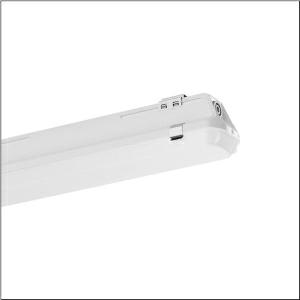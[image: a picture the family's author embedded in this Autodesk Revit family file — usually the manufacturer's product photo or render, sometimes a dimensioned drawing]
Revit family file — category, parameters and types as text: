
# Revit family: monsun_r__21_51fb107p430j005_42d6
name_source: partatom
category: Lighting Fixtures
units: mm (PartAtom-declared; Revit-internal decimal feet)

## family parameters
Cut with Voids When Loaded = No
Host = Face
Light Source = No
Part Type = Normal
Room Calculation Point = No
Round Connector Dimension = Use Diameter
Shared = No

## types (1)
- Monsun® 21 (1 x LED, 3710 lm, 22.2 W, 4000K)
    Apparent Load = 22 VA
    CIE Flux Codes = 47 77 93 94 100
    Color Rendering = 80
    Color Temperature = 4000K
    Default Elevation = 1800 mm
    Description = Monsun® 21, damp-proof luminaire, chain hanger, primary optical cover: enclosure, of PMMA, light emission: direct distribution, primary light characteristic: symmetric, installation type: suspended mounting, surface-mounted, horizontal mounting, vertical mounting, LED, rated luminous flux: 3.710lm, luminous efficacy: 167lm/W, light colour: 840, colour temperature: 4000K, control gear: ECG, with terminal, 3-pole, max. 2.5mm², through-wiring: 5x 2.5mm², mains connection: 220..240V, AC, 50/60Hz, rated input power: 22W, housing, of glass-fibre reinforced polyester, uncoated, bright grey, incl. chain hanger, length: 1.590mm, width: 90mm, height: 88mm, clip for enclosure, of stainless steel (V2A), ceiling mounting element, of stainless steel (V2A), chain hanger, of stainless steel (V2A), protection rating (complete): IP66, insulation class (complete): insulation class I (protective earthing), certification: CE, ENEC, VDE, UKCA, protection symbol: D, impact resistance: IK04, permissible operating ambient temperature: -25..+35°C, standard: EN 50419, EN 60598-2-1, corresponds to IFS (International Featured Standards) requirements for safety and quality in the food industry, for indoor or canopied outdoor use, no direct snow, no direct sun, no direct rain, contact your sales advisor before using the luminaires in applications with unclear chemical exposure, large temperature fluctuations or condensation-forming humidity, LABS conformity tested according to VDMA 24364:2018-05, packaging unit: 1 piece
    Height = 89 mm
    Lamp = 1 x LED
    Lamp Light Flux = 3710 lm
    Lamp Power = 22.2 W
    Lamp count = 1
    Length = 1590 mm
    Luminous efficacy = 167 lm/W
    Manufacturer = Siteco
    ModVariant = No
    Model = 51FB107P430J005
    Mounting Place = Ceiling
    Mounting Type = Surface mounted
    Number of Poles = 1
    OnlyDefault = Yes
    Power Factor = 1
    Product Name = Monsun® 21
    Product group = damp-proof luminaire
    ProductGroupID = 300
    Protection Class = Protection class I
    Protection Degree = IP 66
    RLX_Detail_Level = 1
    RLX_Emergency_Light_Flux = 0 lm
    RLX_Emergency_Type = 0
    RLX_Emergency_Type_DB = No
    RlxData = <blob elided: 88445 chars, md5=d52871f1>
    Socket = socket
    Standby Power = 0 W
    System Light Flux = 3710 lm
    System Power = 22 W
    Type Comments = Product without accessories
    Type Image = l_1006717.jpg
    URL = http://relux.com
    VarID = ---
    Voltage = 0 V
    Weight = 0.00 kg
    Width = 90 mm

## geometry (parser evidence)
native form markers: Blend x4, Sweep x13
no freeform markers — native parametric forms only
